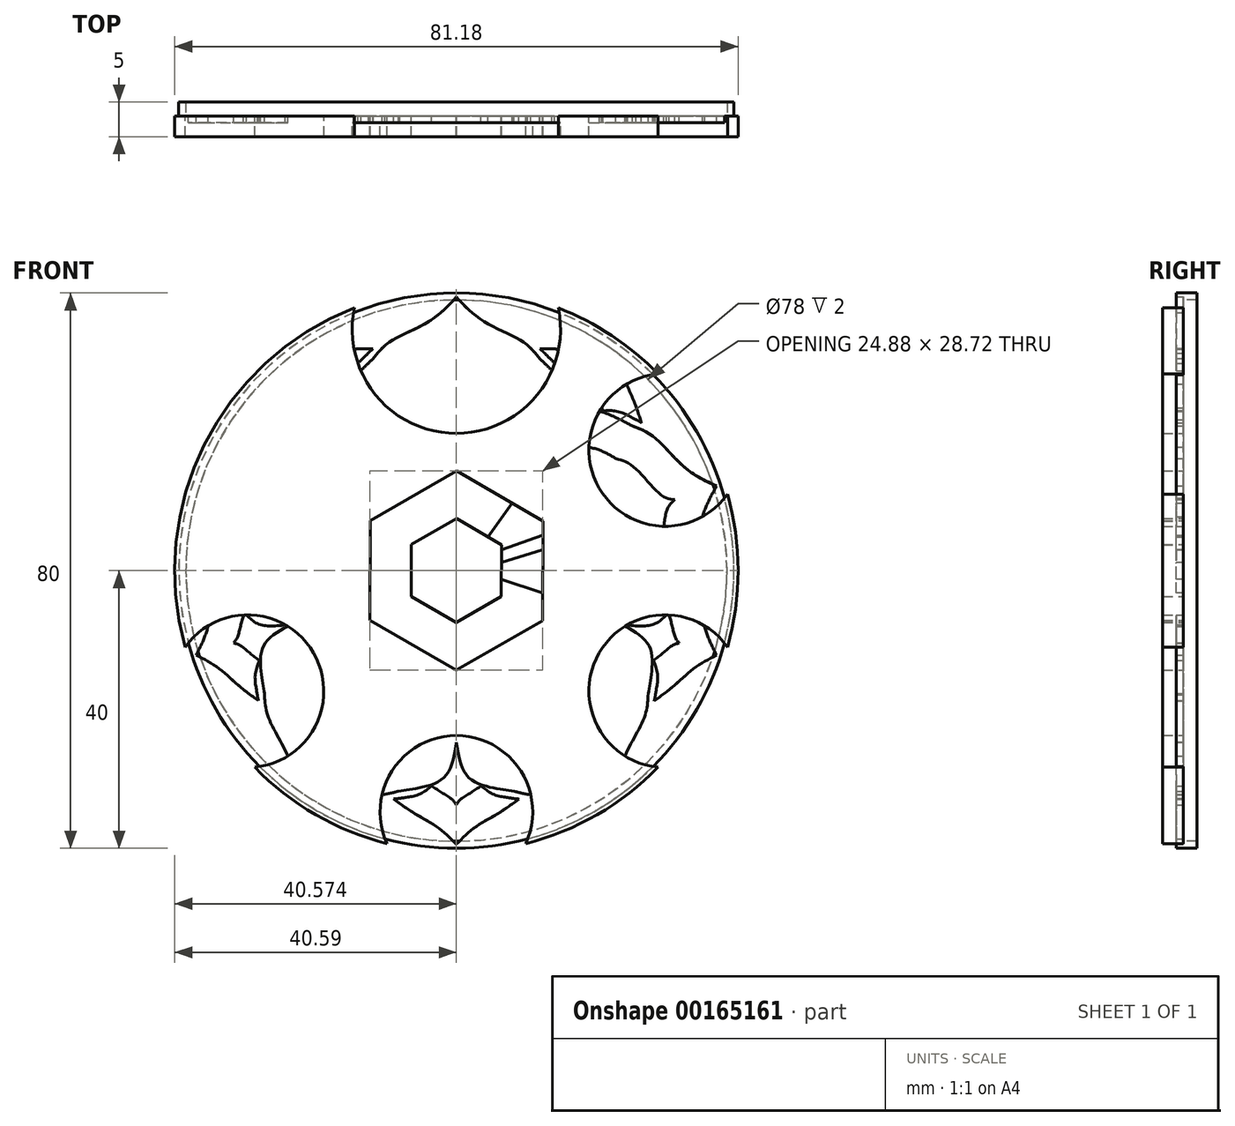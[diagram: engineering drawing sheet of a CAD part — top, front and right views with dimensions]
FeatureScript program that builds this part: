
annotation { "Feature Type Name" : "Feature", "Feature Type Description" : "" }
export const myFeature = defineFeature(function(context is Context, id is Id, definition is map)
    precondition{}
    {
        {
            var Q0;
            Q0=qCreatedBy(makeId("Front.planeOp"),FACE);
            var sketch = newSketch(context, id + "F0", { "sketchPlane" : qUnion([Q0])});
            skFitSpline(sketch, "E0", {"points": [v(12.7, 31.34) * mm, v(12.5, 31.53) * mm, v(12.29, 31.73) * mm, v(12.06, 31.93) * mm]});
            skFitSpline(sketch, "E1", {"points": [v(12.06, 31.93) * mm, v(15.39, 31.86) * mm, v(19.52, 31.52) * mm, v(23.18, 31.9) * mm]});
            skFitSpline(sketch, "E2", {"points": [v(23.18, 31.9) * mm, v(23.95, 28.3) * mm, v(25.56, 24.46) * mm, v(26.65, 21.32) * mm]});
            skFitSpline(sketch, "E3", {"points": [v(26.65, 21.32) * mm, v(26.39, 21.47) * mm, v(26.13, 21.62) * mm, v(25.88, 21.75) * mm]});
            skFitSpline(sketch, "E4", {"points": [v(25.88, 21.75) * mm, v(25.13, 22.14) * mm, v(23.37, 22.9) * mm, v(21.11, 23.01) * mm]});
            skFitSpline(sketch, "E5", {"points": [v(21.11, 23.01) * mm, v(20.46, 24.75) * mm, v(19.87, 26.37) * mm, v(19.85, 27.31) * mm]});
            skFitSpline(sketch, "E6", {"points": [v(19.85, 27.31) * mm, v(18.95, 27.04) * mm, v(17.22, 27.1) * mm, v(15.36, 27.19) * mm]});
            skFitSpline(sketch, "E7", {"points": [v(15.36, 27.19) * mm, v(14.56, 29.3) * mm, v(13.3, 30.74) * mm, v(12.7, 31.34) * mm]});
            skFitSpline(sketch, "E8", {"points": [v(33.73, -2.4) * mm, v(33.85, -2.15) * mm, v(33.97, -1.88) * mm, v(34.09, -1.6) * mm]});
            skFitSpline(sketch, "E9", {"points": [v(34.09, -1.6) * mm, v(35.06, -4.79) * mm, v(36, -8.82) * mm, v(37.5, -12.19) * mm]});
            skFitSpline(sketch, "E10", {"points": [v(37.5, -12.19) * mm, v(34.31, -14.04) * mm, v(31.17, -16.75) * mm, v(28.5, -18.76) * mm]});
            skFitSpline(sketch, "E11", {"points": [v(28.5, -18.76) * mm, v(28.58, -18.46) * mm, v(28.64, -18.17) * mm, v(28.68, -17.9) * mm]});
            skLineSegment(sketch, "E12", {"start": v(25.88, 21.75) * mm, "end": v(25.88, 21.75) * mm});
            skFitSpline(sketch, "E13", {"points": [v(28.68, -17.9) * mm, v(28.82, -17.06) * mm, v(29, -15.15) * mm, v(28.41, -12.97) * mm]});
            skFitSpline(sketch, "E14", {"points": [v(28.41, -12.97) * mm, v(29.86, -11.8) * mm, v(31.22, -10.74) * mm, v(32.11, -10.44) * mm]});
            skFitSpline(sketch, "E15", {"points": [v(32.11, -10.44) * mm, v(31.57, -9.67) * mm, v(31.1, -8) * mm, v(30.6, -6.2) * mm]});
            skFitSpline(sketch, "E16", {"points": [v(30.6, -6.2) * mm, v(32.37, -4.8) * mm, v(33.35, -3.15) * mm, v(33.73, -2.4) * mm]});
            skFitSpline(sketch, "E17", {"points": [v(8.14, -32.82) * mm, v(8.42, -32.86) * mm, v(8.71, -32.89) * mm, v(9.01, -32.91) * mm]});
            skFitSpline(sketch, "E18", {"points": [v(9.01, -32.91) * mm, v(6.28, -34.82) * mm, v(2.73, -36.97) * mm, v(0, -39.43) * mm]});
            skFitSpline(sketch, "E19", {"points": [v(0, -39.43) * mm, v(-2.75, -36.97) * mm, v(-6.3, -34.82) * mm, v(-9.03, -32.9) * mm]});
            skFitSpline(sketch, "E20", {"points": [v(-9.03, -32.9) * mm, v(-8.73, -32.88) * mm, v(-8.43, -32.85) * mm, v(-8.15, -32.8) * mm]});
            skLineSegment(sketch, "E21", {"start": v(28.68, -17.9) * mm, "end": v(28.68, -17.9) * mm});
            skFitSpline(sketch, "E22", {"points": [v(-8.15, -32.8) * mm, v(-7.32, -32.68) * mm, v(-5.45, -32.27) * mm, v(-3.55, -31.03) * mm]});
            skFitSpline(sketch, "E23", {"points": [v(-3.55, -31.03) * mm, v(-2, -32.05) * mm, v(-0.57, -33.01) * mm, v(0, -33.76) * mm]});
            skFitSpline(sketch, "E24", {"points": [v(0, -33.76) * mm, v(0.56, -33.01) * mm, v(2, -32.04) * mm, v(3.55, -31.02) * mm]});
            skFitSpline(sketch, "E25", {"points": [v(3.55, -31.02) * mm, v(5.45, -32.26) * mm, v(7.3, -32.69) * mm, v(8.14, -32.82) * mm]});
            skFitSpline(sketch, "E26", {"points": [v(-28.7, -17.89) * mm, v(-28.65, -18.16) * mm, v(-28.59, -18.45) * mm, v(-28.52, -18.74) * mm]});
            skFitSpline(sketch, "E27", {"points": [v(-28.52, -18.74) * mm, v(-31.18, -16.74) * mm, v(-34.32, -14.03) * mm, v(-37.5, -12.18) * mm]});
            skFitSpline(sketch, "E28", {"points": [v(-37.5, -12.18) * mm, v(-36, -8.8) * mm, v(-35.06, -4.77) * mm, v(-34.09, -1.58) * mm]});
            skFitSpline(sketch, "E29", {"points": [v(-34.09, -1.58) * mm, v(-33.97, -1.86) * mm, v(-33.85, -2.14) * mm, v(-33.72, -2.38) * mm]});
            skLineSegment(sketch, "E30", {"start": v(-8.15, -32.8) * mm, "end": v(-8.15, -32.8) * mm});
            skFitSpline(sketch, "E31", {"points": [v(-33.72, -2.38) * mm, v(-33.34, -3.14) * mm, v(-32.37, -4.79) * mm, v(-30.6, -6.2) * mm]});
            skFitSpline(sketch, "E32", {"points": [v(-30.6, -6.2) * mm, v(-31.1, -8) * mm, v(-31.57, -9.66) * mm, v(-32.11, -10.43) * mm]});
            skFitSpline(sketch, "E33", {"points": [v(-32.11, -10.43) * mm, v(-31.22, -10.74) * mm, v(-29.86, -11.8) * mm, v(-28.4, -12.97) * mm]});
            skFitSpline(sketch, "E34", {"points": [v(-28.4, -12.97) * mm, v(-29, -15.15) * mm, v(-28.83, -17.05) * mm, v(-28.7, -17.89) * mm]});
            skFitSpline(sketch, "E35", {"points": [v(-25.88, 21.76) * mm, v(-26.12, 21.64) * mm, v(-26.38, 21.49) * mm, v(-26.64, 21.33) * mm]});
            skFitSpline(sketch, "E36", {"points": [v(-26.64, 21.33) * mm, v(-25.55, 24.48) * mm, v(-23.94, 28.3) * mm, v(-23.17, 31.9) * mm]});
            skFitSpline(sketch, "E37", {"points": [v(-23.17, 31.9) * mm, v(-19.5, 31.53) * mm, v(-15.37, 31.87) * mm, v(-12.04, 31.93) * mm]});
            skFitSpline(sketch, "E38", {"points": [v(-12.04, 31.93) * mm, v(-12.27, 31.73) * mm, v(-12.5, 31.53) * mm, v(-12.69, 31.34) * mm]});
            skLineSegment(sketch, "E39", {"start": v(-33.72, -2.38) * mm, "end": v(-33.72, -2.38) * mm});
            skFitSpline(sketch, "E40", {"points": [v(-12.69, 31.34) * mm, v(-13.29, 30.74) * mm, v(-14.56, 29.3) * mm, v(-15.36, 27.2) * mm]});
            skFitSpline(sketch, "E41", {"points": [v(-15.36, 27.2) * mm, v(-17.22, 27.1) * mm, v(-18.94, 27.04) * mm, v(-19.84, 27.32) * mm]});
            skFitSpline(sketch, "E42", {"points": [v(-19.84, 27.32) * mm, v(-19.86, 26.38) * mm, v(-20.45, 24.75) * mm, v(-21.1, 23) * mm]});
            skFitSpline(sketch, "E43", {"points": [v(-21.1, 23) * mm, v(-23.37, 22.9) * mm, v(-25.13, 22.15) * mm, v(-25.88, 21.76) * mm]});
            skFitSpline(sketch, "E44", {"points": [v(5.34, 1.73) * mm, v(5.25, 2) * mm, v(5.14, 2.27) * mm, v(5.01, 2.52) * mm]});
            skLineSegment(sketch, "E45", {"start": v(-12.69, 31.34) * mm, "end": v(-12.69, 31.34) * mm});
            skFitSpline(sketch, "E46", {"points": [v(12.7, 5.18) * mm, v(13.23, 5.35) * mm, v(13.8, 5.06) * mm, v(13.98, 4.53) * mm]});
            skFitSpline(sketch, "E47", {"points": [v(13.98, 4.53) * mm, v(14.15, 4) * mm, v(13.86, 3.43) * mm, v(13.33, 3.26) * mm]});
            skLineSegment(sketch, "E48", {"start": v(5.01, 2.52) * mm, "end": v(12.7, 5.18) * mm});
            skFitSpline(sketch, "E49", {"points": [v(5.54, 0.9) * mm, v(5.5, 1.17) * mm, v(5.43, 1.45) * mm, v(5.34, 1.73) * mm]});
            skFitSpline(sketch, "E50", {"points": [v(3.3, -4.55) * mm, v(3.53, -4.37) * mm, v(3.74, -4.19) * mm, v(3.94, -3.99) * mm]});
            skLineSegment(sketch, "E51", {"start": v(13.33, 3.26) * mm, "end": v(5.54, 0.9) * mm});
            skFitSpline(sketch, "E52", {"points": [v(8.85, -10.48) * mm, v(9.18, -10.93) * mm, v(9.08, -11.56) * mm, v(8.63, -11.9) * mm]});
            skFitSpline(sketch, "E53", {"points": [v(8.63, -11.9) * mm, v(8.18, -12.22) * mm, v(7.55, -12.12) * mm, v(7.22, -11.67) * mm]});
            skLineSegment(sketch, "E54", {"start": v(3.94, -3.99) * mm, "end": v(8.85, -10.48) * mm});
            skFitSpline(sketch, "E55", {"points": [v(2.56, -4.99) * mm, v(2.81, -4.86) * mm, v(3.06, -4.72) * mm, v(3.3, -4.55) * mm]});
            skFitSpline(sketch, "E56", {"points": [v(-3.3, -4.54) * mm, v(-3.07, -4.71) * mm, v(-2.82, -4.85) * mm, v(-2.57, -4.98) * mm]});
            skLineSegment(sketch, "E57", {"start": v(7.22, -11.67) * mm, "end": v(2.56, -4.99) * mm});
            skFitSpline(sketch, "E58", {"points": [v(-7.24, -11.66) * mm, v(-7.56, -12.1) * mm, v(-8.2, -12.2) * mm, v(-8.64, -11.88) * mm]});
            skFitSpline(sketch, "E59", {"points": [v(-8.64, -11.88) * mm, v(-9.1, -11.55) * mm, v(-9.2, -10.92) * mm, v(-8.87, -10.47) * mm]});
            skLineSegment(sketch, "E60", {"start": v(-2.57, -4.98) * mm, "end": v(-7.24, -11.66) * mm});
            skFitSpline(sketch, "E61", {"points": [v(-3.95, -3.98) * mm, v(-3.75, -4.18) * mm, v(-3.54, -4.37) * mm, v(-3.3, -4.54) * mm]});
            skFitSpline(sketch, "E62", {"points": [v(-5.34, 1.74) * mm, v(-5.43, 1.46) * mm, v(-5.49, 1.19) * mm, v(-5.53, 0.9) * mm]});
            skLineSegment(sketch, "E63", {"start": v(-8.87, -10.47) * mm, "end": v(-3.95, -3.98) * mm});
            skFitSpline(sketch, "E64", {"points": [v(-13.32, 3.28) * mm, v(-13.85, 3.45) * mm, v(-14.14, 4.02) * mm, v(-13.97, 4.55) * mm]});
            skFitSpline(sketch, "E65", {"points": [v(-13.97, 4.55) * mm, v(-13.8, 5.08) * mm, v(-13.23, 5.37) * mm, v(-12.7, 5.2) * mm]});
            skLineSegment(sketch, "E66", {"start": v(-5.53, 0.9) * mm, "end": v(-13.32, 3.28) * mm});
            skFitSpline(sketch, "E67", {"points": [v(-5, 2.53) * mm, v(-5.13, 2.28) * mm, v(-5.25, 2.02) * mm, v(-5.34, 1.74) * mm]});
            skFitSpline(sketch, "E68", {"points": [v(0, 5.62) * mm, v(-0.29, 5.62) * mm, v(-0.57, 5.59) * mm, v(-0.85, 5.54) * mm]});
            skLineSegment(sketch, "E69", {"start": v(-12.7, 5.2) * mm, "end": v(-5, 2.53) * mm});
            skFitSpline(sketch, "E70", {"points": [v(-1, 13.68) * mm, v(-1, 14.24) * mm, v(-0.55, 14.7) * mm, v(0.01, 14.7) * mm]});
            skFitSpline(sketch, "E71", {"points": [v(0.01, 14.7) * mm, v(0.57, 14.7) * mm, v(1.02, 14.24) * mm, v(1.02, 13.68) * mm]});
            skLineSegment(sketch, "E72", {"start": v(-0.85, 5.54) * mm, "end": v(-1, 13.68) * mm});
            skFitSpline(sketch, "E73", {"points": [v(0.86, 5.54) * mm, v(0.58, 5.59) * mm, v(0.3, 5.62) * mm, v(0, 5.62) * mm]});
            skFitSpline(sketch, "E74", {"points": [v(5.09, 0) * mm, v(5.09, -2.81) * mm, v(2.81, -5.09) * mm, v(0, -5.09) * mm]});
            skFitSpline(sketch, "E75", {"points": [v(0, -5.09) * mm, v(-2.81, -5.09) * mm, v(-5.09, -2.81) * mm, v(-5.09, 0) * mm]});
            skFitSpline(sketch, "E76", {"points": [v(-5.09, 0) * mm, v(-5.09, 2.81) * mm, v(-2.81, 5.09) * mm, v(0, 5.09) * mm]});
            skFitSpline(sketch, "E77", {"points": [v(0, 5.09) * mm, v(2.81, 5.09) * mm, v(5.09, 2.81) * mm, v(5.09, 0) * mm]});
            skFitSpline(sketch, "E78", {"points": [v(31.45, 10.21) * mm, v(30.3, 8.56) * mm, v(29.43, 2.86) * mm, v(28.08, 0.45) * mm]});
            skFitSpline(sketch, "E79", {"points": [v(28.08, 0.45) * mm, v(26.36, -2.64) * mm, v(21, -5.92) * mm, v(12.66, -3.27) * mm]});
            skLineSegment(sketch, "E80", {"start": v(1.02, 13.68) * mm, "end": v(0.86, 5.54) * mm});
            skFitSpline(sketch, "E81", {"points": [v(5.53, -0.96) * mm, v(5.43, -1.5) * mm, v(5.26, -2) * mm, v(5.03, -2.48) * mm]});
            skLineSegment(sketch, "E82", {"start": v(12.66, -3.27) * mm, "end": v(5.53, -0.96) * mm});
            skFitSpline(sketch, "E83", {"points": [v(12.15, -4.8) * mm, v(20.47, -7.56) * mm, v(22.87, -13.37) * mm, v(22.45, -16.87) * mm]});
            skFitSpline(sketch, "E84", {"points": [v(22.45, -16.87) * mm, v(22.12, -19.62) * mm, v(19.46, -24.74) * mm, v(19.43, -26.75) * mm]});
            skFitSpline(sketch, "E85", {"points": [v(19.43, -26.75) * mm, v(17.5, -26.16) * mm, v(11.81, -27.1) * mm, v(9.1, -26.57) * mm]});
            skFitSpline(sketch, "E86", {"points": [v(9.1, -26.57) * mm, v(5.64, -25.89) * mm, v(0.86, -21.8) * mm, v(0.8, -13.05) * mm]});
            skLineSegment(sketch, "E87", {"start": v(5.03, -2.48) * mm, "end": v(12.15, -4.8) * mm});
            skFitSpline(sketch, "E88", {"points": [v(0.8, -5.55) * mm, v(0.53, -5.59) * mm, v(0.27, -5.61) * mm, v(0, -5.61) * mm]});
            skFitSpline(sketch, "E89", {"points": [v(0, -5.61) * mm, v(-0.27, -5.61) * mm, v(-0.54, -5.59) * mm, v(-0.8, -5.55) * mm]});
            skLineSegment(sketch, "E90", {"start": v(0.8, -13.05) * mm, "end": v(0.8, -5.55) * mm});
            skFitSpline(sketch, "E91", {"points": [v(-0.81, -13.04) * mm, v(-0.87, -21.8) * mm, v(-5.65, -25.88) * mm, v(-9.11, -26.57) * mm]});
            skFitSpline(sketch, "E92", {"points": [v(-9.11, -26.57) * mm, v(-11.82, -27.1) * mm, v(-17.52, -26.16) * mm, v(-19.44, -26.74) * mm]});
            skFitSpline(sketch, "E93", {"points": [v(-19.44, -26.74) * mm, v(-19.47, -24.73) * mm, v(-22.13, -19.61) * mm, v(-22.46, -16.87) * mm]});
            skFitSpline(sketch, "E94", {"points": [v(-22.46, -16.87) * mm, v(-22.88, -13.36) * mm, v(-20.48, -7.55) * mm, v(-12.16, -4.8) * mm]});
            skLineSegment(sketch, "E95", {"start": v(-0.8, -5.55) * mm, "end": v(-0.81, -13.04) * mm});
            skFitSpline(sketch, "E96", {"points": [v(-5.03, -2.47) * mm, v(-5.27, -2) * mm, v(-5.44, -1.49) * mm, v(-5.53, -0.95) * mm]});
            skLineSegment(sketch, "E97", {"start": v(-12.16, -4.8) * mm, "end": v(-5.03, -2.47) * mm});
            skFitSpline(sketch, "E98", {"points": [v(-12.65, -3.26) * mm, v(-21, -5.91) * mm, v(-26.36, -2.63) * mm, v(-28.08, 0.46) * mm]});
            skFitSpline(sketch, "E99", {"points": [v(-28.08, 0.46) * mm, v(-29.43, 2.87) * mm, v(-30.29, 8.58) * mm, v(-31.44, 10.22) * mm]});
            skFitSpline(sketch, "E100", {"points": [v(-31.44, 10.22) * mm, v(-29.54, 10.88) * mm, v(-25.5, 14.99) * mm, v(-22.98, 16.15) * mm]});
            skFitSpline(sketch, "E101", {"points": [v(-22.98, 16.15) * mm, v(-19.78, 17.63) * mm, v(-13.51, 17.14) * mm, v(-8.32, 10.08) * mm]});
            skLineSegment(sketch, "E102", {"start": v(-5.53, -0.95) * mm, "end": v(-12.65, -3.26) * mm});
            skFitSpline(sketch, "E103", {"points": [v(-3.9, 4.03) * mm, v(-3.52, 4.4) * mm, v(-3.1, 4.71) * mm, v(-2.62, 4.96) * mm]});
            skLineSegment(sketch, "E104", {"start": v(-8.32, 10.08) * mm, "end": v(-3.9, 4.03) * mm});
            skFitSpline(sketch, "E105", {"points": [v(-7, 11.03) * mm, v(-12.11, 18.15) * mm, v(-10.64, 24.26) * mm, v(-8.24, 26.85) * mm]});
            skFitSpline(sketch, "E106", {"points": [v(-8.24, 26.85) * mm, v(-6.36, 28.87) * mm, v(-1.2, 31.46) * mm, v(0, 33.06) * mm]});
            skFitSpline(sketch, "E107", {"points": [v(0, 33.06) * mm, v(1.22, 31.46) * mm, v(6.38, 28.87) * mm, v(8.25, 26.85) * mm]});
            skFitSpline(sketch, "E108", {"points": [v(8.25, 26.85) * mm, v(10.66, 24.26) * mm, v(12.13, 18.15) * mm, v(7.02, 11.03) * mm]});
            skLineSegment(sketch, "E109", {"start": v(-2.62, 4.96) * mm, "end": v(-7, 11.03) * mm});
            skFitSpline(sketch, "E110", {"points": [v(2.62, 4.96) * mm, v(3.1, 4.71) * mm, v(3.53, 4.4) * mm, v(3.91, 4.02) * mm]});
            skLineSegment(sketch, "E111", {"start": v(7.02, 11.03) * mm, "end": v(2.62, 4.96) * mm});
            skFitSpline(sketch, "E112", {"points": [v(8.32, 10.07) * mm, v(13.52, 17.13) * mm, v(19.78, 17.62) * mm, v(22.99, 16.14) * mm]});
            skFitSpline(sketch, "E113", {"points": [v(22.99, 16.14) * mm, v(25.5, 14.98) * mm, v(29.54, 10.87) * mm, v(31.45, 10.21) * mm]});
            skFitSpline(sketch, "E114", {"points": [v(25.4, 20.82) * mm, v(23.12, 21.99) * mm, v(18.89, 23.05) * mm, v(14.56, 20.02) * mm]});
            skFitSpline(sketch, "E115", {"points": [v(14.56, 20.02) * mm, v(14.55, 20.01) * mm, v(14.54, 20) * mm, v(14.54, 20) * mm]});
            skFitSpline(sketch, "E116", {"points": [v(14.54, 20) * mm, v(14.54, 20) * mm, v(14.55, 20.02) * mm, v(14.55, 20.03) * mm]});
            skFitSpline(sketch, "E117", {"points": [v(14.55, 20.03) * mm, v(16.1, 25.08) * mm, v(13.78, 28.79) * mm, v(11.96, 30.59) * mm]});
            skFitSpline(sketch, "E118", {"points": [v(11.96, 30.59) * mm, v(9.5, 33.03) * mm, v(3.92, 35.92) * mm, v(0, 39.43) * mm]});
            skFitSpline(sketch, "E119", {"points": [v(0, 39.43) * mm, v(-3.91, 35.92) * mm, v(-9.48, 33.03) * mm, v(-11.95, 30.59) * mm]});
            skFitSpline(sketch, "E120", {"points": [v(-11.95, 30.59) * mm, v(-13.77, 28.79) * mm, v(-16.09, 25.08) * mm, v(-14.54, 20.03) * mm]});
            skFitSpline(sketch, "E121", {"points": [v(-14.54, 20.03) * mm, v(-14.54, 20.02) * mm, v(-14.53, 20.01) * mm, v(-14.53, 20) * mm]});
            skFitSpline(sketch, "E122", {"points": [v(-14.53, 20) * mm, v(-14.54, 20.01) * mm, v(-14.55, 20.02) * mm, v(-14.55, 20.03) * mm]});
            skFitSpline(sketch, "E123", {"points": [v(-14.55, 20.03) * mm, v(-18.88, 23.06) * mm, v(-23.12, 22) * mm, v(-25.4, 20.83) * mm]});
            skFitSpline(sketch, "E124", {"points": [v(-25.4, 20.83) * mm, v(-28.48, 19.24) * mm, v(-32.95, 14.83) * mm, v(-37.5, 12.19) * mm]});
            skFitSpline(sketch, "E125", {"points": [v(-37.5, 12.19) * mm, v(-35.37, 7.38) * mm, v(-34.34, 1.19) * mm, v(-32.78, -1.91) * mm]});
            skFitSpline(sketch, "E126", {"points": [v(-32.78, -1.91) * mm, v(-31.63, -4.2) * mm, v(-28.83, -7.55) * mm, v(-23.54, -7.64) * mm]});
            skFitSpline(sketch, "E127", {"points": [v(-23.54, -7.64) * mm, v(-23.54, -7.64) * mm, v(-23.52, -7.64) * mm, v(-23.52, -7.64) * mm]});
            skFitSpline(sketch, "E128", {"points": [v(-23.52, -7.64) * mm, v(-23.52, -7.64) * mm, v(-23.54, -7.65) * mm, v(-23.54, -7.65) * mm]});
            skFitSpline(sketch, "E129", {"points": [v(-23.54, -7.65) * mm, v(-27.77, -10.83) * mm, v(-28.07, -15.2) * mm, v(-27.65, -17.72) * mm]});
            skFitSpline(sketch, "E130", {"points": [v(-27.65, -17.72) * mm, v(-27.1, -21.14) * mm, v(-24.29, -26.75) * mm, v(-23.18, -31.9) * mm]});
            skFitSpline(sketch, "E131", {"points": [v(-23.18, -31.9) * mm, v(-17.95, -31.36) * mm, v(-11.74, -32.3) * mm, v(-8.31, -31.77) * mm]});
            skFitSpline(sketch, "E132", {"points": [v(-8.31, -31.77) * mm, v(-5.78, -31.38) * mm, v(-1.73, -29.75) * mm, v(-0.01, -24.75) * mm]});
            skFitSpline(sketch, "E133", {"points": [v(-0.01, -24.75) * mm, v(0, -24.74) * mm, v(0, -24.73) * mm, v(0, -24.73) * mm]});
            skFitSpline(sketch, "E134", {"points": [v(0, -24.73) * mm, v(0, -24.73) * mm, v(0, -24.75) * mm, v(0, -24.76) * mm]});
            skFitSpline(sketch, "E135", {"points": [v(0, -24.76) * mm, v(1.72, -29.76) * mm, v(5.77, -31.39) * mm, v(8.3, -31.78) * mm]});
            skFitSpline(sketch, "E136", {"points": [v(8.3, -31.78) * mm, v(11.73, -32.3) * mm, v(17.94, -31.36) * mm, v(23.17, -31.9) * mm]});
            skFitSpline(sketch, "E137", {"points": [v(23.17, -31.9) * mm, v(24.28, -26.76) * mm, v(27.09, -21.15) * mm, v(27.65, -17.72) * mm]});
            skFitSpline(sketch, "E138", {"points": [v(27.65, -17.72) * mm, v(28.06, -15.2) * mm, v(27.76, -10.84) * mm, v(23.54, -7.66) * mm]});
            skFitSpline(sketch, "E139", {"points": [v(23.54, -7.66) * mm, v(23.53, -7.65) * mm, v(23.52, -7.65) * mm, v(23.52, -7.65) * mm]});
            skFitSpline(sketch, "E140", {"points": [v(23.52, -7.65) * mm, v(23.52, -7.65) * mm, v(23.54, -7.65) * mm, v(23.54, -7.65) * mm]});
            skFitSpline(sketch, "E141", {"points": [v(23.54, -7.65) * mm, v(28.83, -7.56) * mm, v(31.64, -4.2) * mm, v(32.79, -1.92) * mm]});
            skFitSpline(sketch, "E142", {"points": [v(32.79, -1.92) * mm, v(34.35, 1.18) * mm, v(35.37, 7.37) * mm, v(37.5, 12.18) * mm]});
            skFitSpline(sketch, "E143", {"points": [v(37.5, 12.18) * mm, v(32.95, 14.82) * mm, v(28.48, 19.23) * mm, v(25.4, 20.82) * mm]});
            skLineSegment(sketch, "E144", {"start": v(3.91, 4.02) * mm, "end": v(8.32, 10.07) * mm});
            skCircle(sketch, "E145", {"center": v(0, 0) * mm, "radius": 40 * mm});
            skSolve(sketch);
        }
        {
            var Q0;
            Q0=makeQuery(id+"F0.imprint","IMPRINT",FACE,{"disambiguationData":[TD([[makeQuery(id+"F0.imprint","IMPRINT",EDGE,{"derivedFrom":sQuery(id+"F0.wireOp",EDGE,"E0")}),1.0]])]});
            var Q1;
            Q1=makeQuery(id+"F0.imprint","IMPRINT",FACE,{"disambiguationData":[TD([[makeQuery(id+"F0.imprint","IMPRINT",EDGE,{"derivedFrom":sQuery(id+"F0.wireOp",EDGE,"E44")}),1.0]])]});
            extrude(context, id + "F1", {"entities" : qUnion([Q0, Q1]), "depth" : 1 * mm});
        }
        {
            var Q0;
            Q0=qCreatedBy(makeId("Front.planeOp"),FACE);
            var sketch = newSketch(context, id + "F2", { "sketchPlane" : qUnion([Q0])});
            skCircle(sketch, "E146", {"center": v(0, 0) * mm, "radius": 40 * mm});
            skSolve(sketch);
        }
        {
            var Q0;
            Q0=makeQuery(id+"F2.imprint","IMPRINT",FACE,{"disambiguationData":[TD([[makeQuery(id+"F2.imprint","IMPRINT",EDGE,{"derivedFrom":sQuery(id+"F2.wireOp",EDGE,"E146")}),1.0]])]});
            extrude(context, id + "F3", {"entities" : qUnion([Q0]), "oppositeDirection" : true, "depth" : 2 * mm});
        }
        {
            var Q0;
            Q0=makeQuery(id+"F3.opExtrude","CAP_FACE",FACE,{"disambiguationData":[OSD([sQuery(id+"F2.wireOp",EDGE,"E146")])],"isStart":false});
            var Q1;
            Q1=makeQuery(id+"F3.opExtrude","CAP_FACE",FACE,{"disambiguationData":[OSD([sQuery(id+"F2.wireOp",EDGE,"E146")])],"isStart":true});
            shell(context, id + "F4", {"entities" : qUnion([Q0, Q1]), "thickness" : 1 * mm});
        }
        {
            var Q0;
            Q0=qCreatedBy(makeId("Front.planeOp"),FACE);
            var sketch = newSketch(context, id + "F5", { "sketchPlane" : qUnion([Q0])});
            skCircle(sketch, "E147", {"center": v(0, 34.76) * mm, "radius": 11 * mm});
            skCircle(sketch, "E148.1.0", {"center": v(-30.1, 17.38) * mm, "radius": 11 * mm});
            skCircle(sketch, "E148.2.0", {"center": v(-30.1, -17.38) * mm, "radius": 11 * mm});
            skCircle(sketch, "E148.3.0", {"center": v(0, -34.76) * mm, "radius": 11 * mm});
            skCircle(sketch, "E148.4.0", {"center": v(30.1, -17.38) * mm, "radius": 11 * mm});
            skCircle(sketch, "E148.5.0", {"center": v(30.1, 17.38) * mm, "radius": 11 * mm});
            skPoint(sketch, "E148.center", {"position": v(0, 0) * mm});
            skCircle(sketch, "E149", {"center": v(0, 0) * mm, "radius": 40.6 * mm});
            skCircle(sketch, "E150.0", {"center": v(0, 34.76) * mm, "radius": 15 * mm});
            skCircle(sketch, "E151.cCircle", {"center": v(0, 0) * mm, "radius": 12.43 * mm, "construction": true});
            skLineSegment(sketch, "E151.0", {"start": v(-0.04, -14.36) * mm, "end": v(-12.46, -7.14) * mm});
            skLineSegment(sketch, "E151.1", {"start": v(-12.46, -7.14) * mm, "end": v(-12.41, 7.22) * mm});
            skLineSegment(sketch, "E151.2", {"start": v(-12.41, 7.22) * mm, "end": v(0.04, 14.36) * mm});
            skLineSegment(sketch, "E151.3", {"start": v(0.04, 14.36) * mm, "end": v(12.46, 7.14) * mm});
            skLineSegment(sketch, "E151.4", {"start": v(12.46, 7.14) * mm, "end": v(12.41, -7.22) * mm});
            skLineSegment(sketch, "E151.5", {"start": v(12.41, -7.22) * mm, "end": v(-0.04, -14.36) * mm});
            skPoint(sketch, "E151.0.midPoint", {"position": v(-6.25, -10.75) * mm});
            skLineSegment(sketch, "E152.0", {"start": v(-6.47, 3.76) * mm, "end": v(0.02, 7.48) * mm});
            skLineSegment(sketch, "E152.1", {"start": v(6.5, 3.72) * mm, "end": v(6.47, -3.76) * mm});
            skLineSegment(sketch, "E152.2", {"start": v(6.47, -3.76) * mm, "end": v(-0.02, -7.48) * mm});
            skLineSegment(sketch, "E152.3", {"start": v(0.02, 7.48) * mm, "end": v(6.5, 3.72) * mm});
            skLineSegment(sketch, "E152.4", {"start": v(-0.02, -7.48) * mm, "end": v(-6.5, -3.72) * mm});
            skLineSegment(sketch, "E152.5", {"start": v(-6.5, -3.72) * mm, "end": v(-6.47, 3.76) * mm});
            skSolve(sketch);
        }
        {
            var Q0;
            Q0=makeQuery(id+"F5.imprint","IMPRINT",FACE,{"disambiguationData":[TD([[makeQuery(id+"F5.imprint","IMPRINT",EDGE,{"derivedFrom":sQuery(id+"F5.wireOp",EDGE,"E151.0")}),1.0]])]});
            var Q1;
            Q1=makeQuery(id+"F5.imprint","IMPRINT",FACE,{"disambiguationData":[TD([[makeQuery(id+"F5.imprint","IMPRINT",EDGE,{"derivedFrom":sQuery(id+"F5.wireOp",EDGE,"E152.0")}),-1.0]])]});
            var Q2;
            {var subQ0=sQuery(id+"F5.wireOp",EDGE,"E149");var subQ1=sQuery(id+"F5.wireOp",EDGE,"E148.1.0");var subQ2=makeQuery(id+"F5.imprint","INTERSECT",VERTEX,{"disambiguationData":[OD(0.0)],"derivedFrom":[subQ1,subQ0]});Q2=makeQuery(id+"F5.imprint","IMPRINT",FACE,{"disambiguationData":[TD([[makeQuery(id+"F5.imprint","IMPRINT",EDGE,{"disambiguationData":[TD([[subQ2,1.0]])],"derivedFrom":subQ1}),1.0]])]});}
            extrude(context, id + "F6", {"entities" : qUnion([Q0, Q1, Q2]), "operationType" : NewBodyOperationType.ADD, "depth" : 3 * mm});
        }
    });
